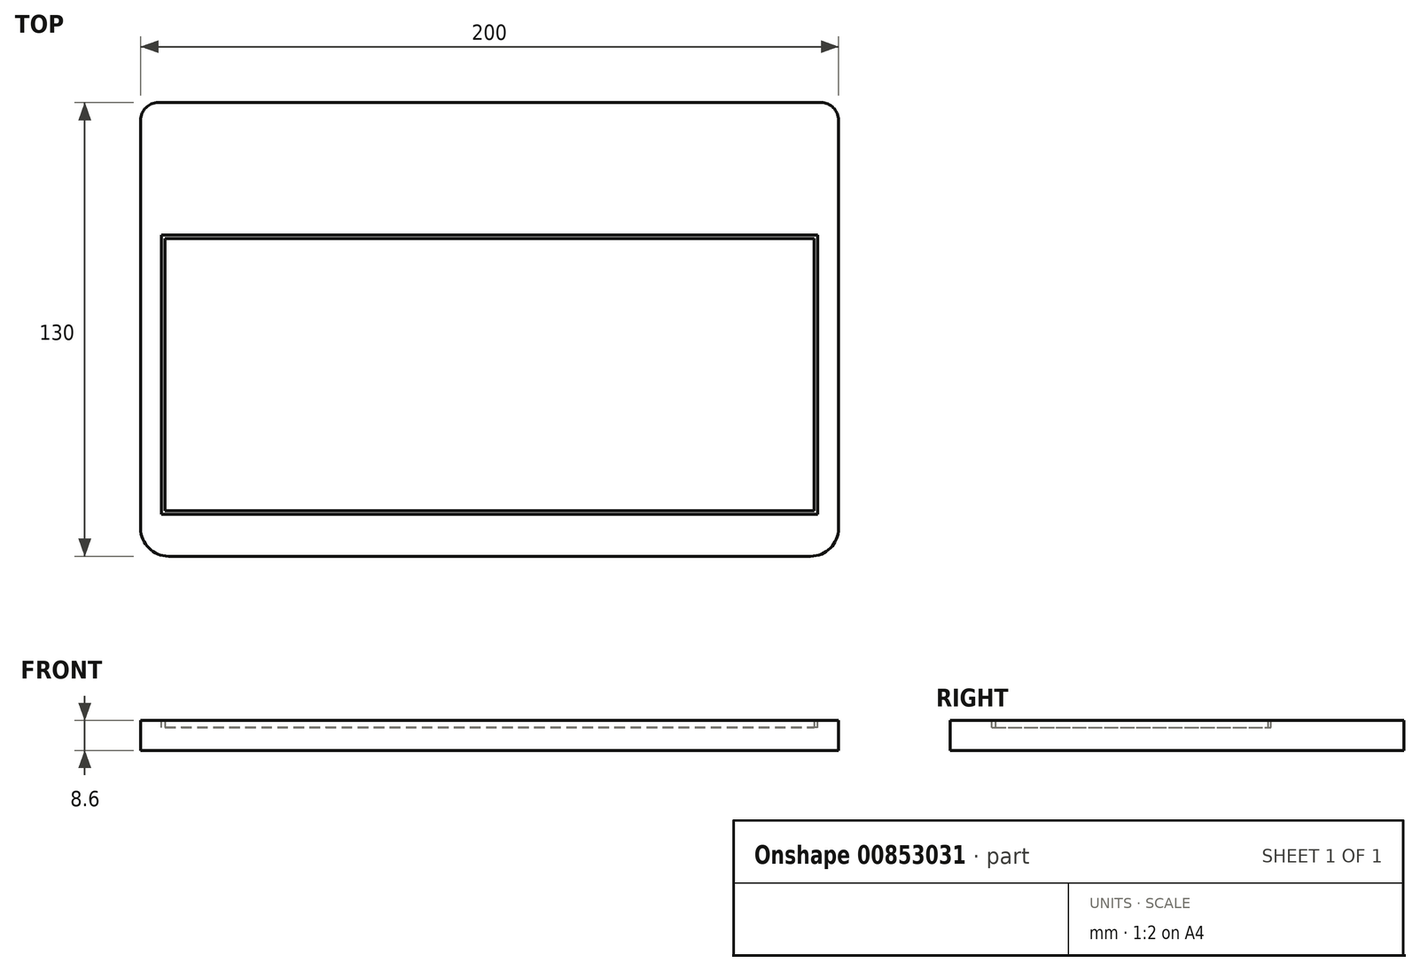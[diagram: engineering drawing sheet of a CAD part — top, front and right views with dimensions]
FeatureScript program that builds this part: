
annotation { "Feature Type Name" : "Feature", "Feature Type Description" : "" }
export const myFeature = defineFeature(function(context is Context, id is Id, definition is map)
    precondition{}
    {
        {
            var Q0;
            Q0=qCreatedBy(makeId("Top.planeOp"),FACE);
            var sketch = newSketch(context, id + "F0", { "sketchPlane" : qUnion([Q0])});
            skLineSegment(sketch, "E0.bottom", {"start": v(100, -65) * mm, "end": v(-100, -65) * mm});
            skLineSegment(sketch, "E0.top", {"start": v(100, 65) * mm, "end": v(-100, 65) * mm});
            skLineSegment(sketch, "E0.left", {"start": v(100, -65) * mm, "end": v(100, 65) * mm});
            skLineSegment(sketch, "E0.right", {"start": v(-100, -65) * mm, "end": v(-100, 65) * mm});
            skPoint(sketch, "E0.middle", {"position": v(0, 0) * mm});
            skSolve(sketch);
        }
        {
            var Q0;
            Q0=makeQuery(id+"F0.imprint","IMPRINT",FACE,{"disambiguationData":[TD([[makeQuery(id+"F0.imprint","IMPRINT",EDGE,{"derivedFrom":sQuery(id+"F0.wireOp",EDGE,"E0.bottom")}),-1.0]])]});
            extrude(context, id + "F1", {"entities" : qUnion([Q0]), "depth" : 8.6 * mm, "offsetDistance" : 25 * mm});
        }
        {
            var Q0;
            Q0=makeQuery(id+"F1.opExtrude","SWEPT_EDGE",EDGE,{"disambiguationData":[OSD([sQuery(id+"F0.wireOp",EDGE,"E0.bottom"),sQuery(id+"F0.wireOp",EDGE,"E0.right")])]});
            var Q1;
            Q1=makeQuery(id+"F1.opExtrude","SWEPT_EDGE",EDGE,{"disambiguationData":[OSD([sQuery(id+"F0.wireOp",EDGE,"E0.bottom"),sQuery(id+"F0.wireOp",EDGE,"E0.left")])]});
            fillet(context, id + "F2", {"entities" : qUnion([Q0, Q1]), "radius" : 8 * mm, "tangentPropagation" : true, "allowEdgeOverflow" : false});
        }
        {
            var Q0;
            Q0=makeQuery(id+"F1.opExtrude","SWEPT_EDGE",EDGE,{"disambiguationData":[OSD([sQuery(id+"F0.wireOp",EDGE,"E0.top"),sQuery(id+"F0.wireOp",EDGE,"E0.left")])]});
            var Q1;
            Q1=makeQuery(id+"F1.opExtrude","SWEPT_EDGE",EDGE,{"disambiguationData":[OSD([sQuery(id+"F0.wireOp",EDGE,"E0.top"),sQuery(id+"F0.wireOp",EDGE,"E0.right")])]});
            fillet(context, id + "F3", {"entities" : qUnion([Q0, Q1]), "radius" : 5 * mm, "tangentPropagation" : true, "allowEdgeOverflow" : false});
        }
        {
            var Q0;
            Q0=makeQuery(id+"F1.opExtrude","CAP_FACE",FACE,{"disambiguationData":[OSD([sQuery(id+"F0.wireOp",EDGE,"E0.bottom"),sQuery(id+"F0.wireOp",EDGE,"E0.top"),sQuery(id+"F0.wireOp",EDGE,"E0.left"),sQuery(id+"F0.wireOp",EDGE,"E0.right")])],"isStart":false});
            var sketch = newSketch(context, id + "F4", { "sketchPlane" : qUnion([Q0])});
            skLineSegment(sketch, "E1.bottom", {"start": v(94, -53) * mm, "end": v(-94, -53) * mm});
            skLineSegment(sketch, "E1.top", {"start": v(94, 27) * mm, "end": v(-94, 27) * mm});
            skLineSegment(sketch, "E1.left", {"start": v(94, -53) * mm, "end": v(94, 27) * mm});
            skLineSegment(sketch, "E1.right", {"start": v(-94, -53) * mm, "end": v(-94, 27) * mm});
            skPoint(sketch, "E1.middle", {"position": v(0, -13) * mm});
            skSolve(sketch);
        }
        {
            var Q0;
            Q0=makeQuery(id+"F4.imprint","IMPRINT",FACE,{"disambiguationData":[TD([[makeQuery(id+"F4.imprint","IMPRINT",EDGE,{"derivedFrom":sQuery(id+"F4.wireOp",EDGE,"E1.bottom")}),-1.0]])]});
            extrude(context, id + "F5", {"entities" : qUnion([Q0]), "operationType" : NewBodyOperationType.REMOVE, "oppositeDirection" : true, "depth" : 2 * mm, "offsetDistance" : 25 * mm});
        }
        {
            var Q0;
            Q0=makeQuery(id+"F5.boolean.opBoolean","COPY",FACE,{"derivedFrom":makeQuery(id+"F5.opExtrude","CAP_FACE",FACE,{"disambiguationData":[OSD([sQuery(id+"F4.wireOp",EDGE,"E1.bottom"),sQuery(id+"F4.wireOp",EDGE,"E1.top"),sQuery(id+"F4.wireOp",EDGE,"E1.left"),sQuery(id+"F4.wireOp",EDGE,"E1.right")])],"isStart":false})});
            var sketch = newSketch(context, id + "F6", { "sketchPlane" : qUnion([Q0])});
            skLineSegment(sketch, "E2.0", {"start": v(93, -52) * mm, "end": v(93, 26) * mm});
            skLineSegment(sketch, "E2.1", {"start": v(-93, -52) * mm, "end": v(93, -52) * mm});
            skLineSegment(sketch, "E2.2", {"start": v(-93, 26) * mm, "end": v(-93, -52) * mm});
            skLineSegment(sketch, "E2.3", {"start": v(93, 26) * mm, "end": v(-93, 26) * mm});
            skSolve(sketch);
        }
        {
            var Q0;
            Q0=makeQuery(id+"F6.imprint","IMPRINT",FACE,{"disambiguationData":[TD([[makeQuery(id+"F6.imprint","IMPRINT",EDGE,{"derivedFrom":sQuery(id+"F6.wireOp",EDGE,"E2.0")}),1.0]])]});
            var Q1;
            Q1=makeQuery(id+"F1.opExtrude","CAP_FACE",FACE,{"disambiguationData":[OSD([sQuery(id+"F0.wireOp",EDGE,"E0.bottom"),sQuery(id+"F0.wireOp",EDGE,"E0.top"),sQuery(id+"F0.wireOp",EDGE,"E0.left"),sQuery(id+"F0.wireOp",EDGE,"E0.right")])],"isStart":false});
            extrude(context, id + "F7", {"entities" : qUnion([Q0]), "operationType" : NewBodyOperationType.ADD, "endBound" : BoundingType.UP_TO_SURFACE, "depth" : 25 * mm, "endBoundEntityFace" : qUnion([Q1]), "offsetDistance" : 25 * mm});
        }
    });
